# Revit family: Electrical_Distribution_ABB_RELIAMOD-400-600A-RELT-MAIN-BRKR
name_source: partatom
category: Electrical Equipment
units: mm (PartAtom-declared; Revit-internal decimal feet)

## family parameters
Cut with Voids When Loaded = No
Host = Face
OmniClass Number = 23.35.29.11
OmniClass Title = Air Circuit Breakers
Panel Configuration = Two Columns, Circuits Across
Part Type = Panelboard
Room Calculation Point = No
Round Connector Dimension = Use Diameter
Shared = No

## types (9) — shared parameters
Apparent Load = 0 VA
Date Updated = 2023/08/25
Default Elevation = 4' - 0"
Enclosure = N3R Outdoor
Feed location = Bottom/Top
Main circuit breaker trip unit = TMA
Main module type = Breaker
Manufacturer = ABB
Primary material = ABB - Steel - White
Product data url = https://www.bimobject.com
URL = https://new.abb.com
Version = 1
zero-valued in all types: Power Factor

## per-type parameters (varying)
| type | Description | Frames | ICRating | Main amperage | Model | Number of Poles | Phase | Voltage | Voltage (V) |
| Default - please load Revit Family Type Catalog | RELIAMOD 1PH 400A 65KAIC MAIN BREAKER | XT5N | 65 | 400 A | RMM1BL4R | 3 | 3-Phase 4-Wire | 208Y/120V | 208 V |
| RMM1BL4R | RELIAMOD 1PH 400A 65KAIC MAIN BREAKER | XT5N | 65 | 400 A | RMM1BL4R | 3 | 3-Phase 4-Wire | 208Y/120V | 208 V |
| RMM1BH4R | RELIAMOD 1PH 400A 100KAIC MAIN BREAKER | XT5S | 100 | 400 A | RMM1BH4R | 2 | 1-Phase 3-Wire | 120/240V | 120 V |
| RMM1BL6R | RELIAMOD 1PH 600A 65KAIC MAIN BREAKER | XT5N | 65 | 600 A | RMM1BL6R | 3 | 3-Phase 4-Wire | 208Y/120V | 208 V |
| RMM1BH6R | RELIAMOD 1PH 600A 100KAIC MAIN BREAKER | XT5S | 100 | 600 A | RMM1BH6R | 2 | 1-Phase 3-Wire | 120/240V | 120 V |
| RMM3BL4R | RELIAMOD 3PH 400A 65KAIC MAIN BREAKER | XT5N | 65 | 400 A | RMM3BL4R | 3 | 3-Phase 4-Wire | 208Y/120V | 208 V |
| RMM3BH4R | RELIAMOD 3PH 400A 100KAIC MAIN BREAKER | XT5S | 100 | 400 A | RMM3BH4R | 2 | 1-Phase 3-Wire | 120/240V | 120 V |
| RMM3BL6R | RELIAMOD 3PH 600A 65KAIC MAIN BREAKER | XT5N | 65 | 600 A | RMM3BL6R | 3 | 3-Phase 4-Wire | 208Y/120V | 208 V |
| RMM3BH6R | RELIAMOD 3PH 600A 100KAIC MAIN BREAKER | XT5S | 100 | 600 A | RMM3BH6R | 2 | 1-Phase 3-Wire | 120/240V | 120 V |

## geometry (parser evidence)
native form markers: Sweep x18
no freeform markers — native parametric forms only
